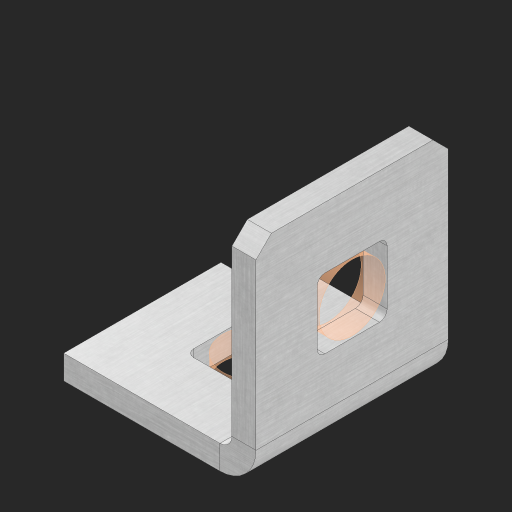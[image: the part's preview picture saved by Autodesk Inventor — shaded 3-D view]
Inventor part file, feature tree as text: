
AUTODESK INVENTOR PART (.ipt)
format: ipt  version: 2023 (Build 270158000, 158)  size: 515,584 bytes
history: native  units: in
note: dims shown in document units (in); Inventor stores cm internally (conversion verified against a paired STEP export)
features: other x153, sheet_metal_op x11, sketch x10, extrude x3, pattern_linear x2, mirror x1, chamfer x1
ambient origin geometry x8: Origin, YZ Plane, XZ Plane, XY Plane, X Axis, Y Axis, Z Axis, Center Point
bodies: Solid1 (feature_tree), Body (feature_tree)
feature tree (181):
  other  "Alu Half C 1x2x1x1"
  other  "Table"
  other  "Alu C 1x2x1x35"
  other  "Alu C 1x2x1x34"
  other  "Alu C 1x2x1x33"
  other  "Alu C 1x2x1x32"
  other  "Alu C 1x2x1x31"
  other  "Alu C 1x2x1x30"
  other  "Alu C 1x2x1x29"
  other  "Alu C 1x2x1x28"
  other  "Alu C 1x2x1x27"
  other  "Alu C 1x2x1x26"
  other  "Alu C 1x2x1x25"
  other  "Alu C 1x2x1x24"
  other  "Alu C 1x2x1x23"
  other  "Alu C 1x2x1x22"
  other  "Alu C 1x2x1x21"
  other  "Alu C 1x2x1x20"
  other  "Alu C 1x2x1x19"
  other  "Alu C 1x2x1x18"
  other  "Alu C 1x2x1x17"
  other  "Alu C 1x2x1x16"
  other  "Alu C 1x2x1x15"
  other  "Alu C 1x2x1x14"
  other  "Alu C 1x2x1x13"
  other  "Alu C 1x2x1x12"
  other  "Alu C 1x2x1x11"
  other  "Alu C 1x2x1x10"
  other  "Alu C 1x2x1x9"
  other  "Alu C 1x2x1x8"
  other  "Alu C 1x2x1x7"
  other  "Alu C 1x2x1x6"
  other  "Alu C 1x2x1x5"
  other  "Alu C 1x2x1x4"
  other  "Alu C 1x2x1x3"
  other  "Alu C 1x2x1x2"
  other  "Alu C 1x2x1x1"
  other  "Steel C 1x2x1x35"
  other  "Steel C 1x2x1x34"
  other  "Steel C 1x2x1x33"
  other  "Steel C 1x2x1x32"
  other  "Steel C 1x2x1x31"
  other  "Steel C 1x2x1x30"
  other  "Steel C 1x2x1x29"
  other  "Steel C 1x2x1x28"
  other  "Steel C 1x2x1x27"
  other  "Steel C 1x2x1x26"
  other  "Steel C 1x2x1x25"
  other  "Steel C 1x2x1x24"
  other  "Steel C 1x2x1x23"
  other  "Steel C 1x2x1x22"
  other  "Steel C 1x2x1x21"
  other  "Steel C 1x2x1x20"
  other  "Steel C 1x2x1x19"
  other  "Steel C 1x2x1x18"
  other  "Steel C 1x2x1x17"
  other  "Steel C 1x2x1x16"
  other  "Steel C 1x2x1x15"
  other  "Steel C 1x2x1x14"
  other  "Steel C 1x2x1x13"
  other  "Steel C 1x2x1x12"
  other  "Steel C 1x2x1x11"
  other  "Steel C 1x2x1x10"
  other  "Steel C 1x2x1x9"
  other  "Steel C 1x2x1x8"
  other  "Steel C 1x2x1x7"
  other  "Steel C 1x2x1x6"
  other  "Steel C 1x2x1x5"
  other  "Steel C 1x2x1x4"
  other  "Steel C 1x2x1x3"
  other  "Steel C 1x2x1x2"
  other  "Steel C 1x2x1x1"
  other  "Alu Half C 1x2x1x35"
  other  "Alu Half C 1x2x1x34"
  other  "Alu Half C 1x2x1x33"
  other  "Alu Half C 1x2x1x32"
  other  "Alu Half C 1x2x1x31"
  other  "Alu Half C 1x2x1x30"
  other  "Alu Half C 1x2x1x29"
  other  "Alu Half C 1x2x1x28"
  other  "Alu Half C 1x2x1x27"
  other  "Alu Half C 1x2x1x26"
  other  "Alu Half C 1x2x1x25"
  other  "Alu Half C 1x2x1x24"
  other  "Alu Half C 1x2x1x23"
  other  "Alu Half C 1x2x1x22"
  other  "Alu Half C 1x2x1x21"
  other  "Alu Half C 1x2x1x20"
  other  "Alu Half C 1x2x1x19"
  other  "Alu Half C 1x2x1x18"
  other  "Alu Half C 1x2x1x17"
  other  "Alu Half C 1x2x1x16"
  other  "Alu Half C 1x2x1x15"
  other  "Alu Half C 1x2x1x14"
  other  "Alu Half C 1x2x1x13"
  other  "Alu Half C 1x2x1x12"
  other  "Alu Half C 1x2x1x11"
  other  "Alu Half C 1x2x1x10"
  other  "Alu Half C 1x2x1x9"
  other  "Alu Half C 1x2x1x8"
  other  "Alu Half C 1x2x1x7"
  other  "Alu Half C 1x2x1x6"
  other  "Alu Half C 1x2x1x5"
  other  "Alu Half C 1x2x1x4"
  other  "Alu Half C 1x2x1x3"
  other  "Alu Half C 1x2x1x2"
  other  "Steel Half C 1x2x1x35"
  other  "Steel Half C 1x2x1x34"
  other  "Steel Half C 1x2x1x33"
  other  "Steel Half C 1x2x1x32"
  other  "Steel Half C 1x2x1x31"
  other  "Steel Half C 1x2x1x30"
  other  "Steel Half C 1x2x1x29"
  other  "Steel Half C 1x2x1x28"
  other  "Steel Half C 1x2x1x27"
  other  "Steel Half C 1x2x1x26"
  other  "Steel Half C 1x2x1x25"
  other  "Steel Half C 1x2x1x24"
  other  "Steel Half C 1x2x1x23"
  other  "Steel Half C 1x2x1x22"
  other  "Steel Half C 1x2x1x21"
  other  "Steel Half C 1x2x1x20"
  other  "Steel Half C 1x2x1x19"
  other  "Steel Half C 1x2x1x18"
  other  "Steel Half C 1x2x1x17"
  other  "Steel Half C 1x2x1x16"
  other  "Steel Half C 1x2x1x15"
  other  "Steel Half C 1x2x1x14"
  other  "Steel Half C 1x2x1x13"
  other  "Steel Half C 1x2x1x12"
  other  "Steel Half C 1x2x1x11"
  other  "Steel Half C 1x2x1x10"
  other  "Steel Half C 1x2x1x9"
  other  "Steel Half C 1x2x1x8"
  other  "Steel Half C 1x2x1x7"
  other  "Steel Half C 1x2x1x6"
  other  "Steel Half C 1x2x1x5"
  other  "Steel Half C 1x2x1x4"
  other  "Steel Half C 1x2x1x3"
  other  "Steel Half C 1x2x1x2"
  other  "Steel Half C 1x2x1x1"
  sheet_metal_op  "Flanges"
  other  "Flange Pattern Plane"
  other  "Flange Pattern Sketch"
  sheet_metal_op  "Flange Pattern"
  sheet_metal_op  "Body Pattern"
  pattern_linear  "Center Pattern"  Spacing1=0.0625in  [1 undecoded]
  other  "Arc Length"
  mirror  "Notch Mirror"
  pattern_linear  "Notch Pattern"  Spacing1=0.182in  [1 undecoded]
  chamfer  "End Chamfer"
  extrude  "Half Cut"  Depth=0.02in
  sketch  "Sketch1"  dims[d0=1.0in]
  other  "Plate1"
  sketch  "Sketch2"  dims[d1=0.5in]
  other  "Plate2"
  sheet_metal_op  "Bend1"
  sheet_metal_op  "Corner1"
  sketch  "Sketch3"  dims[d2=0.0625in]
  sketch  "Sketch7"  dims[d3=0.0625in]
  other  "Srf1"
  other  "Srf2"
  sketch  "Sketch8"  dims[d4=0.0312in]
  sketch  "Sketch9"  dims[d5=0.125in]
  other  "Srf91"
  sheet_metal_op  "Body Pattern Sketch"
  other  "Srf92"
  sketch  "Sketch13"  dims[d6=0.0625in]
  sketch  "Sketch14"  dims[d7=0.5in d8=90.0deg d9=0.0312in]
  sketch  "Sketch15"  dims[d10=0.25in]
  sketch  "Sketch16"  dims[d11=0.0625in d12=0.0625in d16=0.182in d17=0.02in d18=0.0625in d19=0.0in d20=0.25in d21=0.25in d38=0.3937in d40=0.5in d41=0.3937in d43=1.0in d46=0.172in d47=1.0in d48=0.0in d49=0.182in d50=0.02in d51=0.25in d52=0.25in d53=0.0625in d54=0.0in d55=0.172in d56=1.0in d57=0.0in d58=0.25in d60=0.3937in d62=0.5in d63=0.3937in d65=0.5in d85=0.1473in d86=0.1782in d88=0.04in d89=0.0625in d90=0.0in d91=0.04in d92=0.0491in d95=2.5in d96=0.04in d97=0.25in d98=45.0deg d99=0.25in d100=0.5in d101=0.0in d102=2.497in d106=0.182in d107=0.02in d108=0.5in d109=0.5in d110=0.0625in d111=0.0in d112=0.172in d113=0.5in d114=0.0in d117=0.5in d118=0.5in d119=0.5in]
  other  "Srf786"
  sheet_metal_op  "Flange Stamp"
  sheet_metal_op  "Flange Circle"
  sheet_metal_op  "Body Stamp"
  sheet_metal_op  "Body Circle"
  other  "Center Stamp"
  other  "Center Circle"
  sheet_metal_op  "Notch"
  extrude  "ExtrusionSrf2"  Depth=0.0625in
  extrude  "ExtrusionSrf92"  TaperAngle=0.0deg  [1 undecoded]
note: 3 required parameter values undecoded (feature->parameter linkage not recoverable at this tier; creation-order binding heuristic only, values carry confidence <= 0.55)
